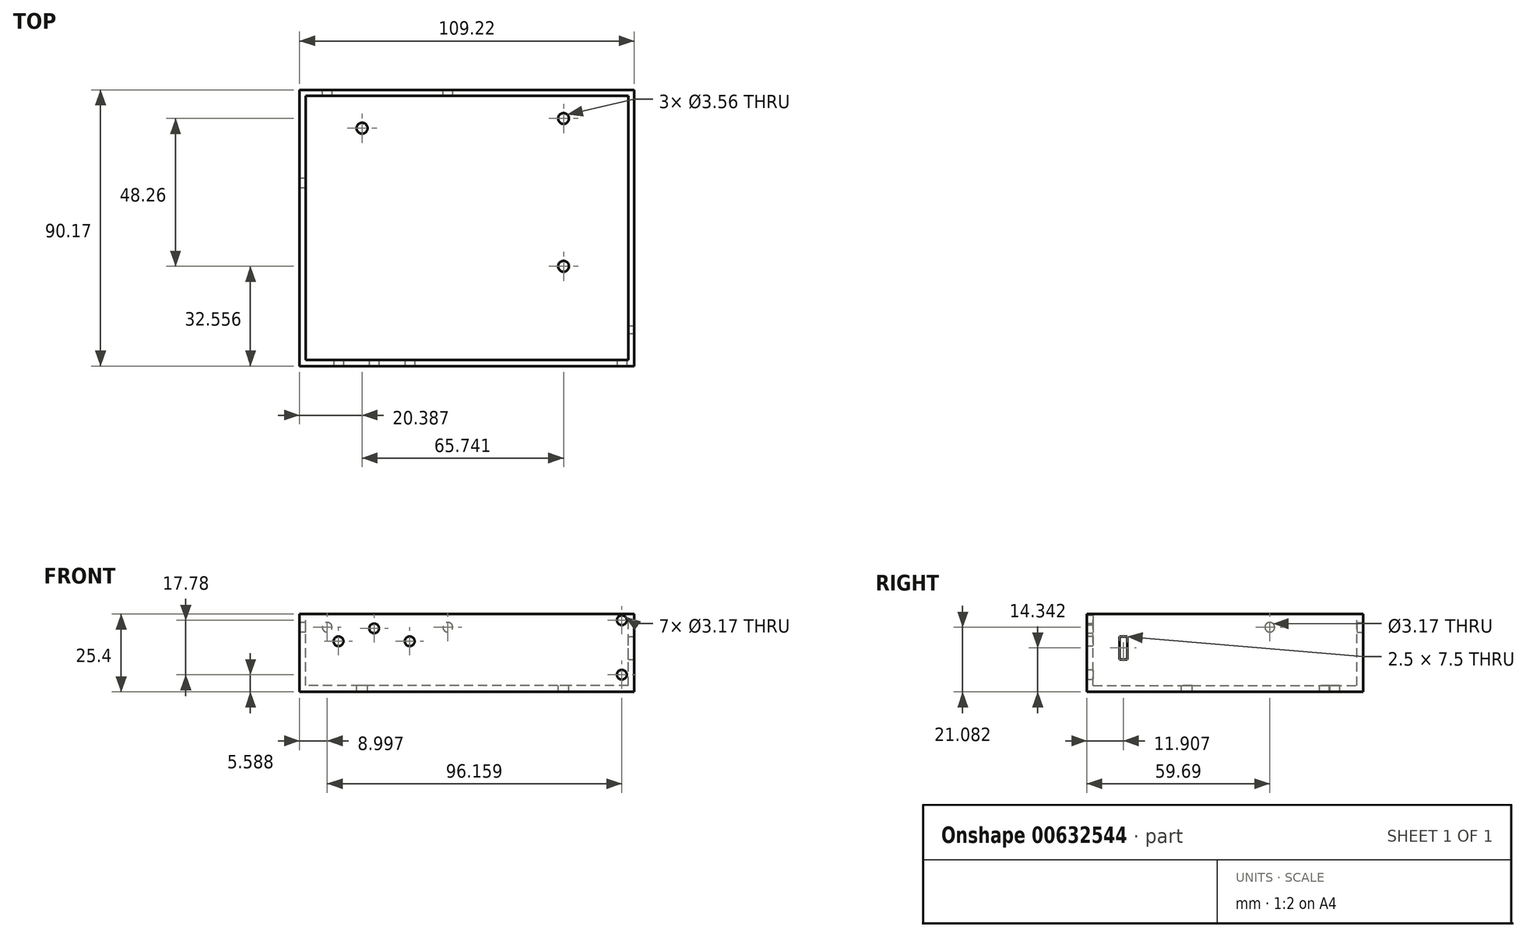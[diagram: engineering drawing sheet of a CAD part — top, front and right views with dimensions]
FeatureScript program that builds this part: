
annotation { "Feature Type Name" : "Feature", "Feature Type Description" : "" }
export const myFeature = defineFeature(function(context is Context, id is Id, definition is map)
    precondition{}
    {
        {
            var Q0;
            Q0=qCreatedBy(makeId("Front.planeOp"),FACE);
            var sketch = newSketch(context, id + "F0", { "sketchPlane" : qUnion([Q0])});
            skLineSegment(sketch, "E0.bottom", {"start": v(54.61, 12.7) * mm, "end": v(-54.6, 12.7) * mm});
            skLineSegment(sketch, "E0.top", {"start": v(54.6, -12.7) * mm, "end": v(-54.61, -12.7) * mm});
            skLineSegment(sketch, "E0.left", {"start": v(54.61, 12.7) * mm, "end": v(54.6, -12.7) * mm});
            skLineSegment(sketch, "E0.right", {"start": v(-54.6, 12.7) * mm, "end": v(-54.61, -12.7) * mm});
            skPoint(sketch, "E0.middle", {"position": v(0, 0) * mm});
            skSolve(sketch);
        }
        {
            var Q0;
            Q0 = qSketchRegion(id + "F0", true);
            extrude(context, id + "F1", {"entities" : qUnion([Q0]), "depth" : 90.17 * mm, "offsetDistance" : 25.4 * mm});
        }
        {
            var Q0;
            Q0=makeQuery(id+"F1.opExtrude","SWEPT_FACE",FACE,{"disambiguationData":[OSD([sQuery(id+"F0.wireOp",EDGE,"E0.bottom")])]});
            var sketch = newSketch(context, id + "F2", { "sketchPlane" : qUnion([Q0])});
            skLineSegment(sketch, "E1.bottom", {"start": v(52.61, -88.17) * mm, "end": v(-52.61, -88.17) * mm});
            skLineSegment(sketch, "E1.top", {"start": v(52.61, -2) * mm, "end": v(-52.61, -2) * mm});
            skLineSegment(sketch, "E1.left", {"start": v(52.61, -88.17) * mm, "end": v(52.61, -2) * mm});
            skLineSegment(sketch, "E1.right", {"start": v(-52.61, -88.17) * mm, "end": v(-52.61, -2) * mm});
            skPoint(sketch, "E1.middle", {"position": v(0, -45.09) * mm});
            skPoint(sketch, "E1.middle.positionSnap0", {"position": v(54.61, -45.09) * mm});
            skPoint(sketch, "E1.centerSnap0", {"position": v(54.61, -45.09) * mm});
            skSolve(sketch);
        }
        {
            var Q0;
            Q0 = qSketchRegion(id + "F2", true);
            extrude(context, id + "F3", {"entities" : qUnion([Q0]), "operationType" : NewBodyOperationType.REMOVE, "oppositeDirection" : true, "depth" : 23.37 * mm, "offsetDistance" : 25.4 * mm});
        }
        {
            var Q0;
            Q0=makeQuery(id+"F1.opExtrude","SWEPT_FACE",FACE,{"disambiguationData":[OSD([sQuery(id+"F0.wireOp",EDGE,"E0.top")])]});
            var sketch = newSketch(context, id + "F4", { "sketchPlane" : qUnion([Q0])});
            skLineSegment(sketch, "E2.bottom", {"start": v(46.99, 82.55) * mm, "end": v(39.37, 82.55) * mm});
            skLineSegment(sketch, "E2.top", {"start": v(46.99, 74.93) * mm, "end": v(39.37, 74.93) * mm});
            skLineSegment(sketch, "E2.left", {"start": v(46.99, 82.55) * mm, "end": v(46.99, 74.93) * mm});
            skLineSegment(sketch, "E2.right", {"start": v(39.37, 82.55) * mm, "end": v(39.37, 74.93) * mm});
            skLineSegment(sketch, "E3.bottom", {"start": v(-39.37, 82.55) * mm, "end": v(-47, 82.55) * mm});
            skLineSegment(sketch, "E3.top", {"start": v(-39.37, 74.93) * mm, "end": v(-47, 74.93) * mm});
            skLineSegment(sketch, "E3.left", {"start": v(-39.37, 82.55) * mm, "end": v(-39.37, 74.93) * mm});
            skLineSegment(sketch, "E3.right", {"start": v(-47, 82.55) * mm, "end": v(-47, 74.93) * mm});
            skLineSegment(sketch, "E4.bottom", {"start": v(46.99, 15.24) * mm, "end": v(39.37, 15.24) * mm});
            skLineSegment(sketch, "E4.top", {"start": v(46.99, 7.62) * mm, "end": v(39.37, 7.62) * mm});
            skLineSegment(sketch, "E4.left", {"start": v(46.99, 15.24) * mm, "end": v(46.99, 7.62) * mm});
            skLineSegment(sketch, "E4.right", {"start": v(39.37, 15.24) * mm, "end": v(39.37, 7.62) * mm});
            skLineSegment(sketch, "E5.bottom", {"start": v(-39.37, 15.24) * mm, "end": v(-47, 15.24) * mm});
            skLineSegment(sketch, "E5.top", {"start": v(-39.37, 7.62) * mm, "end": v(-47, 7.62) * mm});
            skLineSegment(sketch, "E5.left", {"start": v(-39.37, 15.24) * mm, "end": v(-39.37, 7.62) * mm});
            skLineSegment(sketch, "E5.right", {"start": v(-47, 15.24) * mm, "end": v(-47, 7.62) * mm});
            skPoint(sketch, "E6", {"position": v(-43.18, 78.74) * mm});
            skPoint(sketch, "E6.positionSnap0", {"position": v(-43.18, 82.55) * mm});
            skPoint(sketch, "E6.positionSnap1", {"position": v(-47, 78.74) * mm});
            skPoint(sketch, "E7", {"position": v(-43.18, 11.43) * mm});
            skPoint(sketch, "E7.positionSnap0", {"position": v(-47, 11.43) * mm});
            skPoint(sketch, "E7.positionSnap1", {"position": v(-43.18, 15.24) * mm});
            skPoint(sketch, "E8", {"position": v(43.18, 11.43) * mm});
            skPoint(sketch, "E8.positionSnap0", {"position": v(43.18, 15.24) * mm});
            skPoint(sketch, "E8.positionSnap1", {"position": v(39.37, 11.43) * mm});
            skPoint(sketch, "E9", {"position": v(43.18, 78.74) * mm});
            skPoint(sketch, "E9.positionSnap0", {"position": v(39.37, 78.74) * mm});
            skPoint(sketch, "E9.positionSnap1", {"position": v(43.18, 82.55) * mm});
            skSolve(sketch);
        }
        {
            var Q0;
            Q0=makeQuery(id+"F3.boolean.opBoolean","COPY",FACE,{"derivedFrom":makeQuery(id+"F3.opExtrude","CAP_FACE",FACE,{"disambiguationData":[OSD([sQuery(id+"F2.wireOp",EDGE,"E1.bottom"),sQuery(id+"F2.wireOp",EDGE,"E1.top"),sQuery(id+"F2.wireOp",EDGE,"E1.left"),sQuery(id+"F2.wireOp",EDGE,"E1.right")])],"isStart":false})});
            var sketch = newSketch(context, id + "F5", { "sketchPlane" : qUnion([Q0])});
            skLineSegment(sketch, "E10.bottom", {"start": v(-31.68, -15.07) * mm, "end": v(-36.76, -15.07) * mm});
            skLineSegment(sketch, "E10.top", {"start": v(-31.68, -9.99) * mm, "end": v(-36.76, -9.99) * mm});
            skLineSegment(sketch, "E10.left", {"start": v(-31.68, -15.07) * mm, "end": v(-31.68, -9.99) * mm});
            skLineSegment(sketch, "E10.right", {"start": v(-36.76, -15.07) * mm, "end": v(-36.76, -9.99) * mm});
            skPoint(sketch, "E11", {"position": v(-34.22, -12.53) * mm});
            skPoint(sketch, "E11.positionSnap0", {"position": v(-34.22, -9.99) * mm});
            skPoint(sketch, "E11.positionSnap1", {"position": v(-36.76, -12.53) * mm});
            skLineSegment(sketch, "E12.bottom", {"start": v(34.06, -60.15) * mm, "end": v(28.98, -60.15) * mm});
            skLineSegment(sketch, "E12.top", {"start": v(34.06, -55.07) * mm, "end": v(28.98, -55.07) * mm});
            skLineSegment(sketch, "E12.left", {"start": v(34.06, -60.15) * mm, "end": v(34.06, -55.07) * mm});
            skLineSegment(sketch, "E12.right", {"start": v(28.98, -60.15) * mm, "end": v(28.98, -55.07) * mm});
            skPoint(sketch, "E13", {"position": v(31.52, -57.61) * mm});
            skPoint(sketch, "E13.positionSnap0", {"position": v(31.52, -55.07) * mm});
            skPoint(sketch, "E13.positionSnap1", {"position": v(28.98, -57.61) * mm});
            skLineSegment(sketch, "E14.bottom", {"start": v(34.06, -11.9) * mm, "end": v(28.98, -11.9) * mm});
            skLineSegment(sketch, "E14.top", {"start": v(34.06, -6.81) * mm, "end": v(28.98, -6.81) * mm});
            skLineSegment(sketch, "E14.left", {"start": v(34.06, -11.9) * mm, "end": v(34.06, -6.81) * mm});
            skLineSegment(sketch, "E14.right", {"start": v(28.98, -11.9) * mm, "end": v(28.98, -6.81) * mm});
            skPoint(sketch, "E15", {"position": v(31.52, -9.35) * mm});
            skPoint(sketch, "E15.positionSnap0", {"position": v(31.52, -6.81) * mm});
            skPoint(sketch, "E15.positionSnap1", {"position": v(28.98, -9.35) * mm});
            skSolve(sketch);
        }
        {
            var Q0;
            Q0=sQuery(id+"F5.wireOp",VERTEX,"E11");
            var Q1;
            Q1=sQuery(id+"F5.wireOp",VERTEX,"E15");
            var Q2;
            Q2=sQuery(id+"F5.wireOp",VERTEX,"3a233dcb-53d8-4089-b616-3173d63fba25");
            var Q3;
            Q3=sQuery(id+"F5.wireOp",VERTEX,"E13");
            var Q4;
            Q4=makeQuery(id+"F1.opExtrude","SWEPT_BODY",BODY,{"disambiguationData":[OSD([sQuery(id+"F0.wireOp",EDGE,"E0.bottom"),sQuery(id+"F0.wireOp",EDGE,"E0.top"),sQuery(id+"F0.wireOp",EDGE,"E0.left"),sQuery(id+"F0.wireOp",EDGE,"E0.right")])]});
            hole(context, id + "F6", {"style" : HoleStyle.SIMPLE, "endStyle" : HoleEndStyle.THROUGH, "holeDiameter" : 3.56 * mm, "majorDiameter" : 6.35 * mm, "isTappedThrough" : true, "tappedDepth" : 12.7 * mm, "tapClearance" : 3, "locations" : qUnion([Q0, Q1, Q2, Q3]), "scope" : qUnion([Q4])});
        }
        {
            var Q0;
            Q0=sQuery(id+"F5.wireOp",VERTEX,"E13");
            var Q1;
            Q1=makeQuery(id+"F1.opExtrude","SWEPT_BODY",BODY,{"disambiguationData":[OSD([sQuery(id+"F0.wireOp",EDGE,"E0.bottom"),sQuery(id+"F0.wireOp",EDGE,"E0.top"),sQuery(id+"F0.wireOp",EDGE,"E0.left"),sQuery(id+"F0.wireOp",EDGE,"E0.right")])]});
            hole(context, id + "F7", {"style" : HoleStyle.SIMPLE, "endStyle" : HoleEndStyle.THROUGH, "oppositeDirection" : true, "holeDiameter" : 3.17 * mm, "majorDiameter" : 6.35 * mm, "isTappedThrough" : true, "tappedDepth" : 12.7 * mm, "tapClearance" : 3, "locations" : qUnion([Q0]), "scope" : qUnion([Q1])});
        }
        {
            var Q0;
            Q0=makeQuery(id+"F4.imprint","IMPRINT",FACE,{"disambiguationData":[TD([[makeQuery(id+"F4.imprint","IMPRINT",EDGE,{"derivedFrom":sQuery(id+"F4.wireOp",EDGE,"E2.bottom")}),-1.0]])]});
            var sketch = newSketch(context, id + "F10", { "sketchPlane" : qUnion([Q0])});
            skCircle(sketch, "E16", {"center": v(-37.17, 13.92) * mm, "radius": 2.8 * mm});
            skSolve(sketch);
        }
        {
            var Q0;
            Q0 = qSketchRegion(id + "F10", true);
            extrude(context, id + "F11", {"entities" : qUnion([Q0]), "operationType" : NewBodyOperationType.REMOVE, "depth" : 25.4 * mm, "offsetDistance" : 25.4 * mm});
        }
        {
            var Q0;
            Q0=makeQuery(id+"F1.opExtrude","CAP_FACE",FACE,{"disambiguationData":[OSD([sQuery(id+"F0.wireOp",EDGE,"E0.bottom"),sQuery(id+"F0.wireOp",EDGE,"E0.top"),sQuery(id+"F0.wireOp",EDGE,"E0.left"),sQuery(id+"F0.wireOp",EDGE,"E0.right")])],"isStart":false});
            var sketch = newSketch(context, id + "F12", { "sketchPlane" : qUnion([Q0])});
            skPoint(sketch, "E17", {"position": v(50.55, 10.67) * mm});
            skPoint(sketch, "E18", {"position": v(50.55, -7.11) * mm});
            skSolve(sketch);
        }
        {
            var Q0;
            Q0=sQuery(id+"F12.wireOp",VERTEX,"E17");
            var Q1;
            Q1=sQuery(id+"F12.wireOp",VERTEX,"E18");
            var Q2;
            Q2=makeQuery(id+"F1.opExtrude","SWEPT_BODY",BODY,{"disambiguationData":[OSD([sQuery(id+"F0.wireOp",EDGE,"E0.bottom"),sQuery(id+"F0.wireOp",EDGE,"E0.top"),sQuery(id+"F0.wireOp",EDGE,"E0.left"),sQuery(id+"F0.wireOp",EDGE,"E0.right")])]});
            hole(context, id + "F13", {"style" : HoleStyle.SIMPLE, "endStyle" : HoleEndStyle.BLIND, "holeDiameter" : 3.17 * mm, "majorDiameter" : 6.35 * mm, "holeDepth" : 12.7 * mm, "isTappedThrough" : true, "tappedDepth" : 12.7 * mm, "tapClearance" : 3, "locations" : qUnion([Q0, Q1]), "scope" : qUnion([Q2])});
        }
        {
            var Q0;
            Q0=makeQuery(id+"F1.opExtrude","SWEPT_FACE",FACE,{"disambiguationData":[OSD([sQuery(id+"F0.wireOp",EDGE,"E0.left")])]});
            var sketch = newSketch(context, id + "F14", { "sketchPlane" : qUnion([Q0])});
            skLineSegment(sketch, "E19.bottom", {"start": v(-77.01, -2.1) * mm, "end": v(-79.51, -2.1) * mm});
            skLineSegment(sketch, "E19.top", {"start": v(-77.01, 5.4) * mm, "end": v(-79.51, 5.4) * mm});
            skLineSegment(sketch, "E19.left", {"start": v(-77.01, -2.1) * mm, "end": v(-77.01, 5.4) * mm});
            skLineSegment(sketch, "E19.right", {"start": v(-79.51, -2.1) * mm, "end": v(-79.51, 5.4) * mm});
            skSolve(sketch);
        }
        {
            var Q0;
            Q0=makeQuery(id+"F14.imprint","IMPRINT",FACE,{"disambiguationData":[TD([[makeQuery(id+"F14.imprint","IMPRINT",EDGE,{"derivedFrom":sQuery(id+"F14.wireOp",EDGE,"E19.bottom")}),-1.0]])]});
            extrude(context, id + "F15", {"entities" : qUnion([Q0]), "operationType" : NewBodyOperationType.REMOVE, "oppositeDirection" : true, "depth" : 5.08 * mm, "offsetDistance" : 25.4 * mm});
        }
        {
            var Q0;
            Q0=makeQuery(id+"F0.imprint","IMPRINT",FACE,{"disambiguationData":[TD([[makeQuery(id+"F0.imprint","IMPRINT",EDGE,{"derivedFrom":sQuery(id+"F0.wireOp",EDGE,"E0.bottom")}),1.0]])]});
            var sketch = newSketch(context, id + "F16", { "sketchPlane" : qUnion([Q0])});
            skPoint(sketch, "E20", {"position": v(-6.24, 8.38) * mm});
            skPoint(sketch, "E21", {"position": v(-45.61, 8.38) * mm});
            skSolve(sketch);
        }
        {
            var Q0;
            Q0=sQuery(id+"F16.wireOp",VERTEX,"E20");
            var Q1;
            Q1=sQuery(id+"F16.wireOp",VERTEX,"E21");
            var Q2;
            Q2=makeQuery(id+"F1.opExtrude","SWEPT_BODY",BODY,{"disambiguationData":[OSD([sQuery(id+"F0.wireOp",EDGE,"E0.bottom"),sQuery(id+"F0.wireOp",EDGE,"E0.top"),sQuery(id+"F0.wireOp",EDGE,"E0.left"),sQuery(id+"F0.wireOp",EDGE,"E0.right")])]});
            hole(context, id + "F17", {"style" : HoleStyle.SIMPLE, "endStyle" : HoleEndStyle.BLIND, "oppositeDirection" : true, "holeDiameter" : 3.17 * mm, "majorDiameter" : 6.35 * mm, "holeDepth" : 12.7 * mm, "isTappedThrough" : true, "tappedDepth" : 12.7 * mm, "tapClearance" : 3, "locations" : qUnion([Q0, Q1]), "scope" : qUnion([Q2])});
        }
        {
            var Q0;
            Q0=makeQuery(id+"F1.opExtrude","SWEPT_FACE",FACE,{"disambiguationData":[OSD([sQuery(id+"F0.wireOp",EDGE,"E0.right")])]});
            var sketch = newSketch(context, id + "F18", { "sketchPlane" : qUnion([Q0])});
            skPoint(sketch, "E22", {"position": v(30.48, 8.38) * mm});
            skSolve(sketch);
        }
        {
            var Q0;
            Q0=sQuery(id+"F18.wireOp",VERTEX,"E22");
            var Q1;
            Q1=makeQuery(id+"F1.opExtrude","SWEPT_BODY",BODY,{"disambiguationData":[OSD([sQuery(id+"F0.wireOp",EDGE,"E0.bottom"),sQuery(id+"F0.wireOp",EDGE,"E0.top"),sQuery(id+"F0.wireOp",EDGE,"E0.left"),sQuery(id+"F0.wireOp",EDGE,"E0.right")])]});
            hole(context, id + "F19", {"style" : HoleStyle.SIMPLE, "endStyle" : HoleEndStyle.BLIND, "holeDiameter" : 3.17 * mm, "majorDiameter" : 6.35 * mm, "holeDepth" : 12.7 * mm, "isTappedThrough" : true, "tappedDepth" : 12.7 * mm, "tapClearance" : 3, "locations" : qUnion([Q0]), "scope" : qUnion([Q1])});
        }
        {
            var Q0;
            Q0=makeQuery(id+"F1.opExtrude","CAP_FACE",FACE,{"disambiguationData":[OSD([sQuery(id+"F0.wireOp",EDGE,"E0.bottom"),sQuery(id+"F0.wireOp",EDGE,"E0.top"),sQuery(id+"F0.wireOp",EDGE,"E0.left"),sQuery(id+"F0.wireOp",EDGE,"E0.right")])],"isStart":false});
            var sketch = newSketch(context, id + "F20", { "sketchPlane" : qUnion([Q0])});
            skPoint(sketch, "E23", {"position": v(-41.91, 3.8) * mm});
            skPoint(sketch, "E24", {"position": v(-18.67, 3.8) * mm});
            skPoint(sketch, "E25", {"position": v(-30.29, 8) * mm});
            skSolve(sketch);
        }
        {
            var Q0;
            Q0=sQuery(id+"F20.wireOp",VERTEX,"E25");
            var Q1;
            Q1=sQuery(id+"F20.wireOp",VERTEX,"E23");
            var Q2;
            Q2=sQuery(id+"F20.wireOp",VERTEX,"E24");
            var Q3;
            Q3=makeQuery(id+"F1.opExtrude","SWEPT_BODY",BODY,{"disambiguationData":[OSD([sQuery(id+"F0.wireOp",EDGE,"E0.bottom"),sQuery(id+"F0.wireOp",EDGE,"E0.top"),sQuery(id+"F0.wireOp",EDGE,"E0.left"),sQuery(id+"F0.wireOp",EDGE,"E0.right")])]});
            hole(context, id + "F21", {"style" : HoleStyle.SIMPLE, "endStyle" : HoleEndStyle.BLIND, "holeDiameter" : 3.17 * mm, "majorDiameter" : 6.35 * mm, "holeDepth" : 12.7 * mm, "isTappedThrough" : true, "tappedDepth" : 12.7 * mm, "tapClearance" : 3, "locations" : qUnion([Q0, Q1, Q2]), "scope" : qUnion([Q3])});
        }
    });
